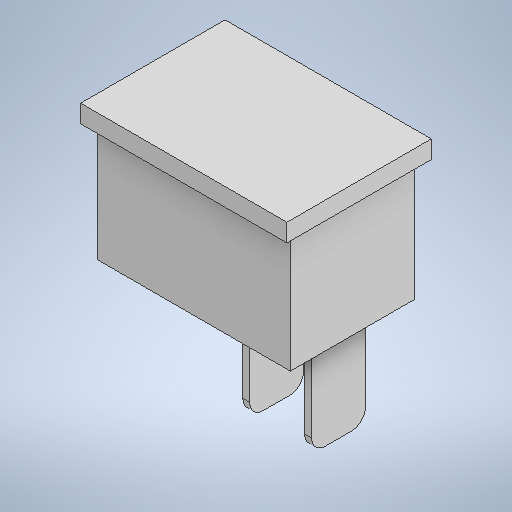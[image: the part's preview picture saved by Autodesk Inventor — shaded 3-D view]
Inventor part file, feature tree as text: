
AUTODESK INVENTOR PART (.ipt)
format: ipt  version: 2025.1 (Build 291241000, 241)  size: 246,272 bytes
history: native  units: mm
features: extrude x3, sketch x3, other x1, fillet x1
ambient origin geometry x8: Origin, YZ Plane, XZ Plane, XY Plane, X Axis, Y Axis, Z Axis, Center Point
bodies: Body1 (feature_tree)
feature tree (8):
  other  "ソリッド1"
  extrude  "押し出し1"  Depth=14.0mm
  extrude  "押し出し2"  Depth=9.0mm
  extrude  "押し出し3"  Depth=8.7mm TaperAngle=0.0deg
  fillet  "フィレット1"  Radius=10.5mm
  sketch  "スケッチ1"
  sketch  "スケッチ2"
  sketch  "スケッチ3"
